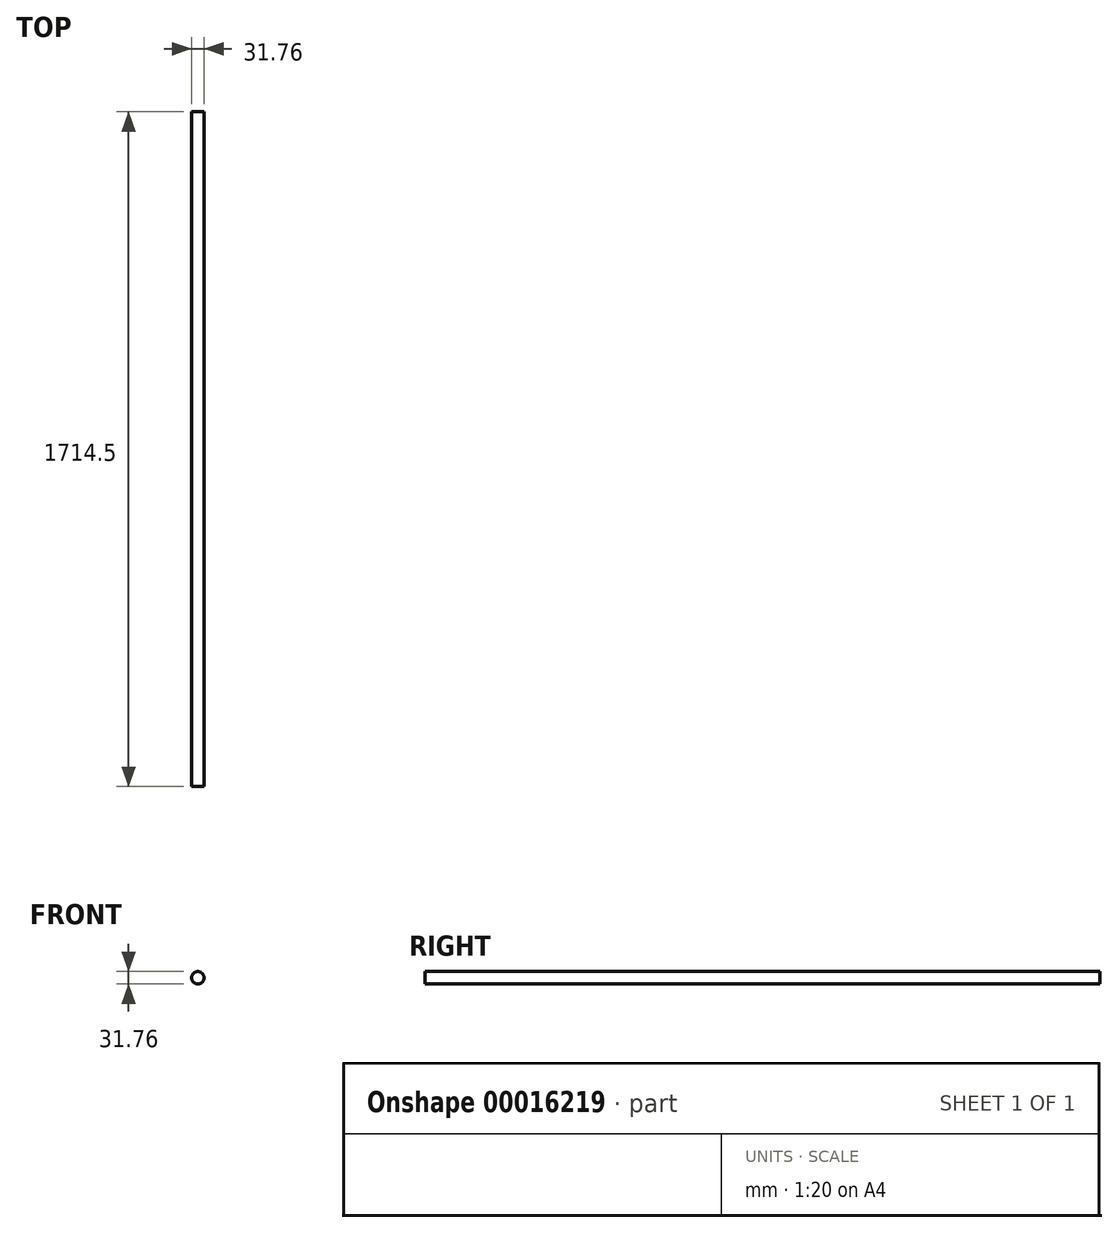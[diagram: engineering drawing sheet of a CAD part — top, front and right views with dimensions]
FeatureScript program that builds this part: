
annotation { "Feature Type Name" : "Feature", "Feature Type Description" : "" }
export const myFeature = defineFeature(function(context is Context, id is Id, definition is map)
    precondition{}
    {
        {
            var Q0;
            Q0=qCreatedBy(makeId("Right.planeOp"),FACE);
            var sketch = newSketch(context, id + "F0", { "sketchPlane" : qUnion([Q0])});
            skLineSegment(sketch, "E0", {"start": v(0, 0) * mm, "end": v(-1714.5, 0) * mm});
            skSolve(sketch);
        }
        {
            var Q0;
            Q0=qCreatedBy(makeId("Front.planeOp"),FACE);
            var sketch = newSketch(context, id + "F1", { "sketchPlane" : qUnion([Q0])});
            skCircle(sketch, "E1", {"center": v(0, 0) * mm, "radius": 15.88 * mm});
            skSolve(sketch);
        }
        {
            var Q0;
            Q0=makeQuery(id+"F1.imprint","IMPRINT",FACE,{"disambiguationData":[TD([[makeQuery(id+"F1.imprint","IMPRINT",EDGE,{"derivedFrom":sQuery(id+"F1.wireOp",EDGE,"E1")}),1.0]])]});
            var Q1;
            Q1=sQuery(id+"F0.wireOp",EDGE,"E0");
            sweep(context, id + "F2", {"profiles" : qUnion([Q0]), "path" : qUnion([Q1])});
        }
    });
